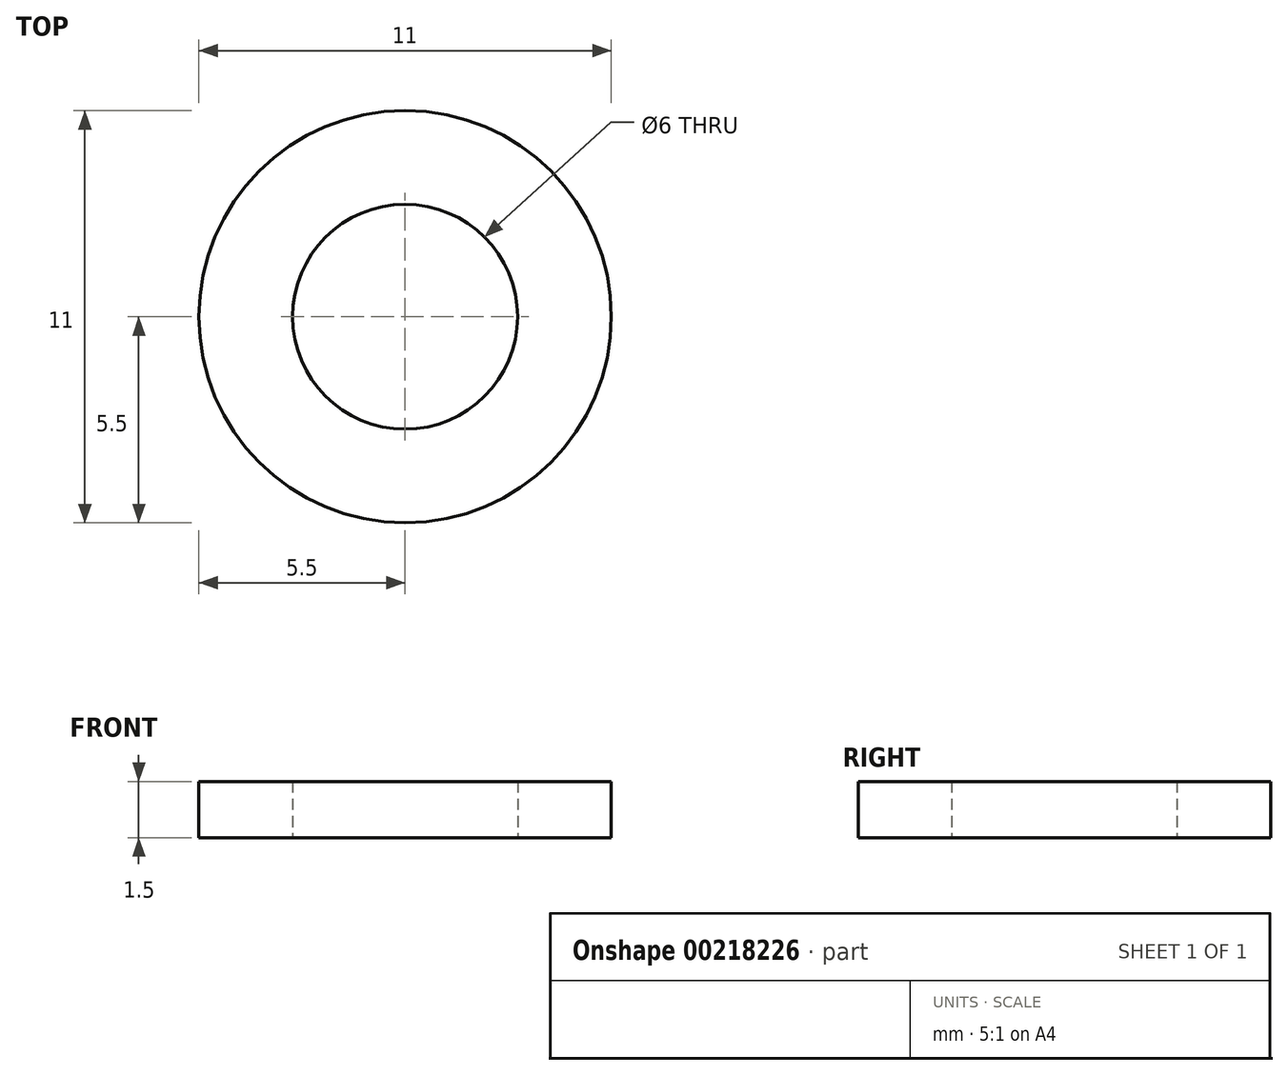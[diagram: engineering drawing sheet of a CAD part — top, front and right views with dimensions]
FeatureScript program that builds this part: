
annotation { "Feature Type Name" : "Feature", "Feature Type Description" : "" }
export const myFeature = defineFeature(function(context is Context, id is Id, definition is map)
    precondition{}
    {
        {
            var Q0;
            Q0=qCreatedBy(makeId("Top.planeOp"),FACE);
            var sketch = newSketch(context, id + "F0", { "sketchPlane" : qUnion([Q0])});
            skCircle(sketch, "E0", {"center": v(0, 0) * mm, "radius": 3 * mm});
            skCircle(sketch, "E1", {"center": v(0, 0) * mm, "radius": 5.5 * mm});
            skSolve(sketch);
        }
        {
            var Q0;
            Q0 = qSketchRegion(id + "F0", true);
            extrude(context, id + "F1", {"entities" : qUnion([Q0]), "depth" : 1.5 * mm});
        }
    });
